# Revit family: 02 - EVO235 - 200 DIS
name_source: partatom
category: Mechanical Equipment
revit_build: Autodesk Revit 2018 (Build: 20170223_1515(x64)
units: mm (PartAtom-declared; Revit-internal decimal feet)

## family parameters
Always vertical = Yes
Cut with Voids When Loaded = No
Host = Ceiling
OmniClass Number = 23.75.00.00
OmniClass Title = Climate Control (HVAC)
Part Type = Normal
Room Calculation Point = No
Round Connector Dimension = Use Diameter
Shared = No

## types (20) — shared parameters
Access Clearance Bottom = 150 mm
Access Clearance Front = 300 mm
Access Clearance Left = 150 mm
Access Clearance Rear = 300 mm
Access Clearance Right = 150 mm
Air Flow Rate = 0.0 L/s
Assembly Code = D3050100
CHW Flow Temp. = 0
CHW Return Temp. = 0 °C
Ch.W Coil Connection Size = 15 mm  [stored 0.0492126 ft]
Ch.W Coil Flow = 0.0 L/s
Con Pan Length = 156 mm  [stored 0.511811 ft]
Condensate Drain Connection Size = 15 mm  [stored 0.0492126 ft]
Condensate Drain Max Flow = 0.0 L/s
Condensate Tray = Yes
Configuration = Horizontal
Control Valves & Actuators = No
Controls Connection = No
Cooling Coil Duty (Sensible) = 0 W
Cooling Coil Duty (Total) = 0 W
Description = Ceiling Mounted 235mm Deep Horizontal Fan Coil Unit
Drain Connection Size = 15 mm  [stored 0.0492126 ft]
Drain Cut Size = 13 mm  [stored 0.0426509 ft]
Earth Connector = Yes
Electrical Enclosure Depth = 215 mm
Electrical Enclosure Height = 210 mm
Electrical Enclosure Width = 350 mm  [stored 1.14829 ft]
Electrical Power Consumption = 0 W
Electrical Supply Current (Max) = 0 A
Enclosure Depth (Model) = 213.8 mm  [stored 0.701444 ft]
Enclosure Height (Model) = 208.8 mm  [stored 0.685039 ft]
FCU Depth = 235 mm  [stored 0.770997 ft]
FCU Length = 900 mm
Fan Type = Double Inlet Centrifugal
Heating Coil Duty Range = 0 W
Incoming Supply Electrical Frequency = 50 Hz
Incoming Supply Electrical Voltage = 230 V
Incoming Supply Phase = 1
Inlet Plenum = No
Intake Height = 205 mm
LPHW Flow Temperature = 0 °C
LPHW Return Temp. = 0 °C
LTHW Coil Connection Size = 15 mm  [stored 0.0492126 ft]
LTHW Coil Flow = 0.0 L/s
Low Voltage Transformer = No
Manufacturer = Ability Projects
Mat Thickness Neg = -1.2 mm  [stored -0.00393701 ft]
Mat Thickness Pos = 1.2 mm  [stored 0.00393701 ft]
Max Ext Press. = 0.0 Pa
Model = EVO235
Motor Enclosure Rating = IP42
Motor Type = EC
Operating Weight = 0.00 kg
Outlet Connection Dia/Height = 200 mm  [stored 0.656168 ft]
Outlet Connection Shape = Circular
Overall Height = 235 mm  [stored 0.770997 ft]
Overall Length = 900 mm
Pipe Connection Type = Screw
Primary Filter = G3
Return Air Temperature Sensor = No
Room Air Temperature Sensor = No
Shipping Weight = 0.00 kg
Speed Selection Controller = No
Starting Method = Soft Start
Summer Fresh Air Temp. = 0 °C
Summer On Coil Temp. = 0 °C
Summer Room Temp. = 0 °C
Summer off Coil Temp. = 0 °C
Temperature Controller = No
URL = http://www.abilityprojects.com
Winter Fresh Air Temp. = 0 °C
Winter On Coil Temp. = 0 °C
Winter Room Temp. = 0 °C
Winter off Coil Temp. = 0 °C
∆P Cooling Coil = 0.0 Pa
∆P Htg Coil = 0.0 Pa
zero-valued in all types: Access Clearance Top, Con Pan Extension, Inlet Connection Dia/Height, Inlet Connection Width, Outlet Connection Width, Sound Transmission (NR), Specific Fan Power

## per-type parameters (varying)
| type | Circular Spigot No | Circular Spigot Position | Circular Spigot Spacing | FCU Width | Handing | Intake Width | LH Components Visible | Left Side Clearance | No of Outlet Connections | Overall Width | RH Components Visible | Right Side Clearance |
| EVO235 - Size 100 LH | 1 | 308 mm  [stored 1.0105 ft] | 555 mm  [stored 1.82087 ft] | 616 mm  [stored 2.021 ft] | LH | 530 mm | Yes | 336 mm  [stored 1.10236 ft] | 3 | 802 mm | No | 10 mm  [stored 0.0328084 ft] |
| EVO235 - Size 100 RH | 1 | 308 mm  [stored 1.0105 ft] | 555 mm  [stored 1.82087 ft] | 616 mm  [stored 2.021 ft] | RH | 530 mm | No | 10 mm  [stored 0.0328084 ft] | 3 | 802 mm | Yes | 336 mm  [stored 1.10236 ft] |
| EVO235 - Size 200 LH | 2 | 243 mm | 430 mm | 916 mm | LH | 830 mm | Yes | 336 mm  [stored 1.10236 ft] | 4 | 1102 mm | No | 10 mm  [stored 0.0328084 ft] |
| EVO235 - Size 200 RH | 2 | 243 mm | 430 mm | 916 mm | RH | 830 mm | No | 10 mm  [stored 0.0328084 ft] | 4 | 1102 mm | Yes | 336 mm  [stored 1.10236 ft] |
| EVO235 - Size 250 LH | 2 | 243 mm | 430 mm | 916 mm | LH | 830 mm | Yes | 336 mm  [stored 1.10236 ft] | 4 | 1102 mm | No | 10 mm  [stored 0.0328084 ft] |
| EVO235 - Size 250 RH | 2 | 243 mm | 430 mm | 916 mm | RH | 830 mm | No | 10 mm  [stored 0.0328084 ft] | 4 | 1102 mm | Yes | 336 mm  [stored 1.10236 ft] |
| EVO235 - Size 300 LH | 3 | 223 mm | 385 mm  [stored 1.26312 ft] | 1216 mm | LH | 1130 mm | Yes | 336 mm  [stored 1.10236 ft] | 5 | 1402 mm | No | 10 mm  [stored 0.0328084 ft] |
| EVO235 - Size 300 RH | 3 | 223 mm | 385 mm  [stored 1.26312 ft] | 1216 mm | RH | 1130 mm | No | 10 mm  [stored 0.0328084 ft] | 5 | 1402 mm | Yes | 336 mm  [stored 1.10236 ft] |
| EVO235 - Size 350 LH | 3 | 223 mm | 385 mm  [stored 1.26312 ft] | 1216 mm | LH | 1130 mm | Yes | 336 mm  [stored 1.10236 ft] | 5 | 1402 mm | No | 10 mm  [stored 0.0328084 ft] |
| EVO235 - Size 350 RH | 3 | 223 mm | 385 mm  [stored 1.26312 ft] | 1216 mm | RH | 1130 mm | No | 10 mm  [stored 0.0328084 ft] | 5 | 1402 mm | Yes | 336 mm  [stored 1.10236 ft] |
| EVO235 - Size 400 LH | 4 | 210.5 mm | 365 mm | 1516 mm | LH | 1430 mm | Yes | 336 mm  [stored 1.10236 ft] | 6 | 1702 mm | No | 10 mm  [stored 0.0328084 ft] |
| EVO235 - Size 400 RH | 4 | 210.5 mm | 365 mm | 1516 mm | RH | 1430 mm | No | 10 mm  [stored 0.0328084 ft] | 6 | 1702 mm | Yes | 336 mm  [stored 1.10236 ft] |
| EVO235 - Size 500 LH | 4 | 248 mm | 440 mm  [stored 1.44357 ft] | 1816 mm | LH | 1730 mm | Yes | 336 mm  [stored 1.10236 ft] | 6 | 2002 mm | No | 10 mm  [stored 0.0328084 ft] |
| EVO235 - Size 500 RH | 4 | 248 mm | 440 mm  [stored 1.44357 ft] | 1816 mm | RH | 1730 mm | No | 10 mm  [stored 0.0328084 ft] | 6 | 2002 mm | Yes | 336 mm  [stored 1.10236 ft] |
| EVO235 - Size 550 LH | 4 | 248 mm | 440 mm  [stored 1.44357 ft] | 1816 mm | LH | 1730 mm | Yes | 336 mm  [stored 1.10236 ft] | 6 | 2002 mm | No | 10 mm  [stored 0.0328084 ft] |
| EVO235 - Size 550 RH | 4 | 248 mm | 440 mm  [stored 1.44357 ft] | 1816 mm | RH | 1730 mm | No | 10 mm  [stored 0.0328084 ft] | 6 | 2002 mm | Yes | 336 mm  [stored 1.10236 ft] |
| EVO235 - Size 600 LH | 5 | 238 mm | 410 mm | 2116 mm | LH | 2030 mm | Yes | 336 mm  [stored 1.10236 ft] | 7 | 2302 mm | No | 10 mm  [stored 0.0328084 ft] |
| EVO235 - Size 600 RH | 5 | 238 mm | 410 mm | 2116 mm | RH | 2030 mm | No | 10 mm  [stored 0.0328084 ft] | 7 | 2302 mm | Yes | 336 mm  [stored 1.10236 ft] |
| EVO235 - Size 650 LH | 5 | 238 mm | 410 mm | 2116 mm | LH | 2030 mm | Yes | 336 mm  [stored 1.10236 ft] | 7 | 2302 mm | No | 10 mm  [stored 0.0328084 ft] |
| EVO235 - Size 650 RH | 5 | 238 mm | 410 mm | 2116 mm | RH | 2030 mm | No | 10 mm  [stored 0.0328084 ft] | 7 | 2302 mm | Yes | 336 mm  [stored 1.10236 ft] |

note: source unit labels omitted for CHW Flow Temp. — the stored unit's dimension contradicts the parameter name (converter mislabeling)

note: [stored X ft] marks values corroborated as IEEE doubles in the binary element streams (Revit-internal decimal feet)

## geometry (parser evidence)
native form markers: Sweep x8
no freeform markers — native parametric forms only
